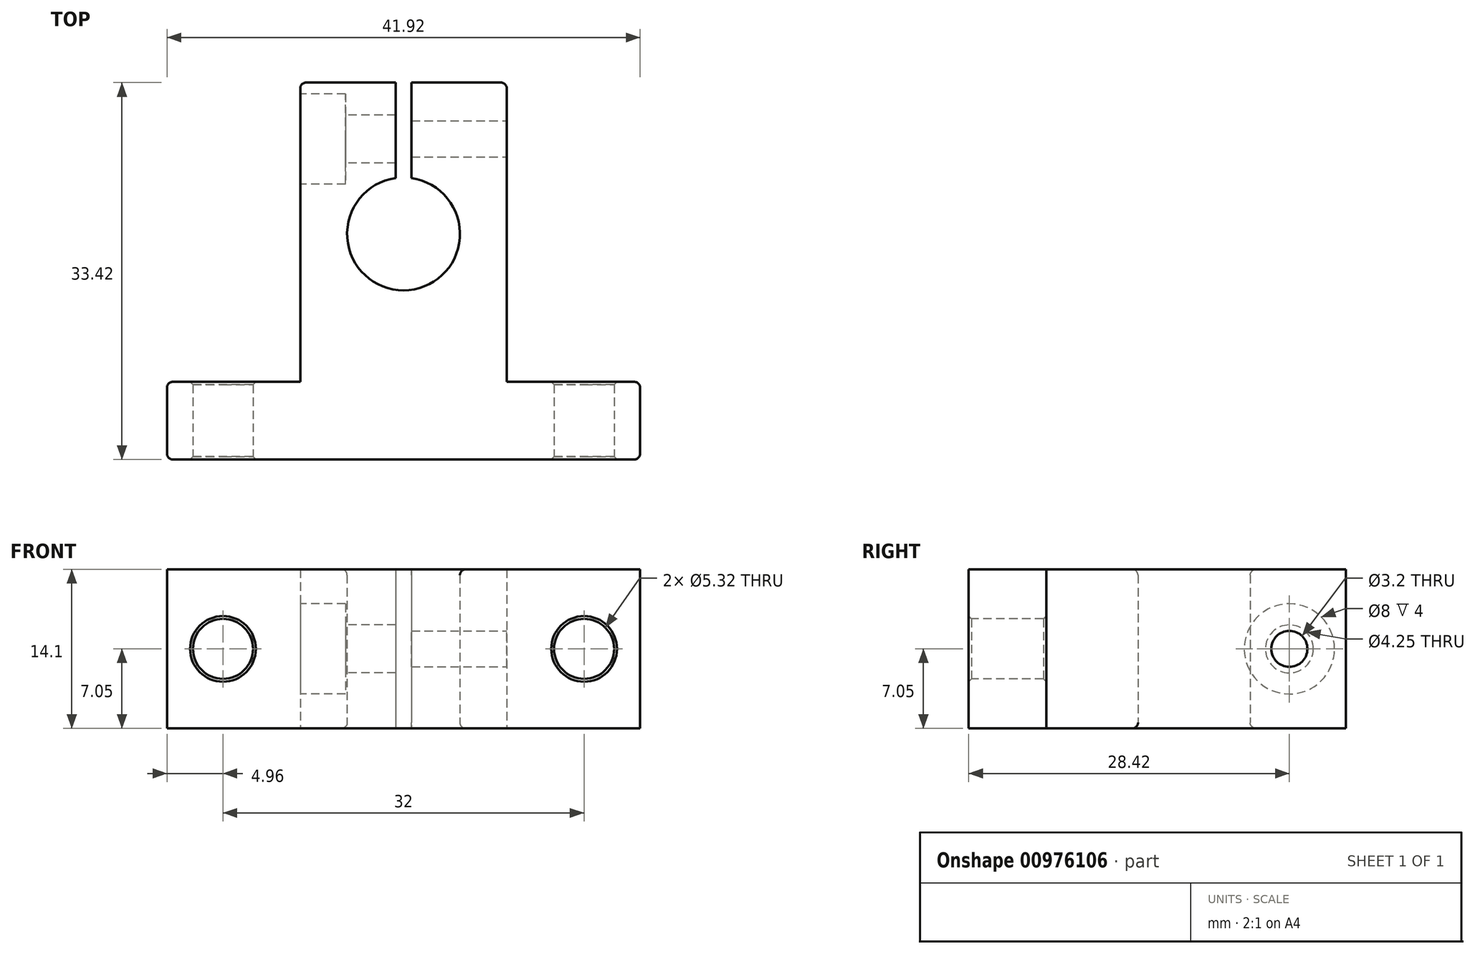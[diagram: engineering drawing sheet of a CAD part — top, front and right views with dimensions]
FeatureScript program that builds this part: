
annotation { "Feature Type Name" : "Feature", "Feature Type Description" : "" }
export const myFeature = defineFeature(function(context is Context, id is Id, definition is map)
    precondition{}
    {
        {
            var Q0;
            Q0=qCreatedBy(makeId("Top.planeOp"),FACE);
            var sketch = newSketch(context, id + "F0", { "sketchPlane" : qUnion([Q0])});
            skArc(sketch, "E0", {"start": v(-0.7, 4.95) * mm, "mid": v(0, -5) * mm, "end": v(0.7, 4.95) * mm});
            skLineSegment(sketch, "E1.bottom", {"start": v(-9.15, 13.42) * mm, "end": v(-0.7, 13.42) * mm});
            skLineSegment(sketch, "E1.left", {"start": v(-9.15, 13.42) * mm, "end": v(-9.15, -13.12) * mm});
            skLineSegment(sketch, "E1.right", {"start": v(9.15, 13.42) * mm, "end": v(9.15, -13.12) * mm});
            skLineSegment(sketch, "E2.bottom", {"start": v(-20.96, -13.12) * mm, "end": v(-9.15, -13.12) * mm});
            skLineSegment(sketch, "E2.top", {"start": v(-20.96, -20) * mm, "end": v(20.96, -20) * mm});
            skLineSegment(sketch, "E2.left", {"start": v(-20.96, -13.12) * mm, "end": v(-20.96, -20) * mm});
            skLineSegment(sketch, "E2.right", {"start": v(20.96, -13.12) * mm, "end": v(20.96, -20) * mm});
            skLineSegment(sketch, "E3.trimOffspring", {"start": v(9.15, -13.12) * mm, "end": v(20.96, -13.12) * mm});
            skLineSegment(sketch, "E4", {"start": v(0, 0) * mm, "end": v(0, 13.42) * mm, "construction": true});
            skLineSegment(sketch, "E5", {"start": v(0, 0) * mm, "end": v(0, -20) * mm, "construction": true});
            skLineSegment(sketch, "E6", {"start": v(-0.7, 4.95) * mm, "end": v(-0.7, 13.42) * mm});
            skLineSegment(sketch, "E7", {"start": v(0.7, 13.42) * mm, "end": v(0.7, 4.95) * mm});
            skLineSegment(sketch, "E8.trimOffspring", {"start": v(0.7, 13.42) * mm, "end": v(9.15, 13.42) * mm});
            skLineSegment(sketch, "E9", {"start": v(-0.7, 13.42) * mm, "end": v(0.7, 13.42) * mm, "construction": true});
            skSolve(sketch);
        }
        {
            var Q0;
            Q0 = qSketchRegion(id + "F0", true);
            extrude(context, id + "F1", {"entities" : qUnion([Q0]), "depth" : 14.1 * mm, "offsetDistance" : 25 * mm});
        }
        {
            var Q0;
            Q0=makeQuery(id+"F1.opExtrude","SWEPT_FACE",FACE,{"disambiguationData":[OSD([sQuery(id+"F0.wireOp",EDGE,"E1.right")])]});
            var sketch = newSketch(context, id + "F2", { "sketchPlane" : qUnion([Q0])});
            skLineSegment(sketch, "E10", {"start": v(8.42, 14.1) * mm, "end": v(8.42, 0) * mm, "construction": true});
            skCircle(sketch, "E11", {"center": v(8.42, 7.05) * mm, "radius": 1.6 * mm});
            skSolve(sketch);
        }
        {
            var Q0;
            Q0 = qSketchRegion(id + "F2", true);
            extrude(context, id + "F3", {"entities" : qUnion([Q0]), "operationType" : NewBodyOperationType.REMOVE, "endBound" : BoundingType.THROUGH_ALL, "oppositeDirection" : true, "depth" : 25 * mm, "offsetDistance" : 25 * mm});
        }
        {
            var Q0;
            Q0=makeQuery(id+"F1.opExtrude","SWEPT_FACE",FACE,{"disambiguationData":[OSD([sQuery(id+"F0.wireOp",EDGE,"E1.left")])]});
            var sketch = newSketch(context, id + "F4", { "sketchPlane" : qUnion([Q0])});
            skCircle(sketch, "E12", {"center": v(-8.42, 7.05) * mm, "radius": 4 * mm});
            skSolve(sketch);
        }
        {
            var Q0;
            Q0 = qSketchRegion(id + "F4", true);
            extrude(context, id + "F5", {"entities" : qUnion([Q0]), "operationType" : NewBodyOperationType.REMOVE, "oppositeDirection" : true, "depth" : 4 * mm, "offsetDistance" : 25 * mm});
        }
        {
            var Q0;
            Q0=makeQuery(id+"F1.opExtrude","SWEPT_FACE",FACE,{"disambiguationData":[OSD([sQuery(id+"F0.wireOp",EDGE,"E2.top")])]});
            var sketch = newSketch(context, id + "F6", { "sketchPlane" : qUnion([Q0])});
            skLineSegment(sketch, "E13", {"start": v(-20.96, 7.05) * mm, "end": v(-16, 7.05) * mm, "construction": true});
            skLineSegment(sketch, "E14", {"start": v(-16, 7.05) * mm, "end": v(16, 7.05) * mm, "construction": true});
            skLineSegment(sketch, "E15", {"start": v(16, 7.05) * mm, "end": v(20.96, 7.05) * mm, "construction": true});
            skCircle(sketch, "E16", {"center": v(-16, 7.05) * mm, "radius": 2.66 * mm});
            skCircle(sketch, "E17", {"center": v(16, 7.05) * mm, "radius": 2.66 * mm});
            skSolve(sketch);
        }
        {
            var Q0;
            Q0 = qSketchRegion(id + "F6", true);
            extrude(context, id + "F7", {"entities" : qUnion([Q0]), "operationType" : NewBodyOperationType.REMOVE, "oppositeDirection" : true, "depth" : 25 * mm, "offsetDistance" : 25 * mm});
        }
        {
            var Q0;
            Q0=makeQuery(id+"F5.boolean.opBoolean","COPY",FACE,{"derivedFrom":makeQuery(id+"F5.opExtrude","CAP_FACE",FACE,{"disambiguationData":[OSD([sQuery(id+"F4.wireOp",EDGE,"E12")])],"isStart":false})});
            var sketch = newSketch(context, id + "F8", { "sketchPlane" : qUnion([Q0])});
            skCircle(sketch, "E18", {"center": v(-8.42, 7.05) * mm, "radius": 2.12 * mm});
            skSolve(sketch);
        }
        {
            var Q0;
            Q0 = qSketchRegion(id + "F8", true);
            var Q1;
            Q1=makeQuery(id+"F1.opExtrude","SWEPT_FACE",FACE,{"disambiguationData":[OSD([sQuery(id+"F0.wireOp",EDGE,"E7")])]});
            extrude(context, id + "F9", {"entities" : qUnion([Q0]), "operationType" : NewBodyOperationType.REMOVE, "endBound" : BoundingType.UP_TO_SURFACE, "oppositeDirection" : true, "depth" : 25 * mm, "endBoundEntityFace" : qUnion([Q1]), "offsetDistance" : 25 * mm});
        }
        {
            var Q0;
            Q0=makeQuery(id+"F1.opExtrude","SWEPT_EDGE",EDGE,{"disambiguationData":[OSD([sQuery(id+"F0.wireOp",EDGE,"E2.bottom"),sQuery(id+"F0.wireOp",EDGE,"E2.left")])]});
            var Q1;
            Q1=makeQuery(id+"F1.opExtrude","SWEPT_EDGE",EDGE,{"disambiguationData":[OSD([sQuery(id+"F0.wireOp",EDGE,"E2.top"),sQuery(id+"F0.wireOp",EDGE,"E2.left")])]});
            var Q2;
            Q2=makeQuery(id+"F1.opExtrude","SWEPT_EDGE",EDGE,{"disambiguationData":[OSD([sQuery(id+"F0.wireOp",EDGE,"E2.right"),sQuery(id+"F0.wireOp",EDGE,"E3.trimOffspring")])]});
            var Q3;
            Q3=makeQuery(id+"F1.opExtrude","SWEPT_EDGE",EDGE,{"disambiguationData":[OSD([sQuery(id+"F0.wireOp",EDGE,"E2.top"),sQuery(id+"F0.wireOp",EDGE,"E2.right")])]});
            var Q4;
            Q4=makeQuery(id+"F1.opExtrude","SWEPT_EDGE",EDGE,{"disambiguationData":[OSD([sQuery(id+"F0.wireOp",EDGE,"E1.right"),sQuery(id+"F0.wireOp",EDGE,"E8.trimOffspring")])]});
            var Q5;
            Q5=makeQuery(id+"F1.opExtrude","SWEPT_EDGE",EDGE,{"disambiguationData":[OSD([sQuery(id+"F0.wireOp",EDGE,"E1.bottom"),sQuery(id+"F0.wireOp",EDGE,"E1.left")])]});
            var Q6;
            Q6=makeQuery(id+"F1.opExtrude","CAP_EDGE",EDGE,{"disambiguationData":[OSD([sQuery(id+"F0.wireOp",EDGE,"E0")])],"isStart":false});
            var Q7;
            Q7=makeQuery(id+"F1.opExtrude","CAP_EDGE",EDGE,{"disambiguationData":[OSD([sQuery(id+"F0.wireOp",EDGE,"E0")])],"isStart":true});
            fillet(context, id + "F10", {"entities" : qUnion([Q0, Q1, Q2, Q3, Q4, Q5, Q6, Q7]), "radius" : .5 * mm, "tangentPropagation" : true, "allowEdgeOverflow" : false});
        }
        {
            var Q0;
            Q0=makeQuery(id+"F7.boolean.opBoolean","COPY",FACE,{"derivedFrom":makeQuery(id+"F7.opExtrude","SWEPT_FACE",FACE,{"disambiguationData":[OSD([sQuery(id+"F6.wireOp",EDGE,"E17")])]})});
            var Q1;
            Q1=makeQuery(id+"F7.boolean.opBoolean","COPY",FACE,{"derivedFrom":makeQuery(id+"F7.opExtrude","SWEPT_FACE",FACE,{"disambiguationData":[OSD([sQuery(id+"F6.wireOp",EDGE,"E16")])]})});
            chamfer(context, id + "F11", {"entities" : qUnion([Q0, Q1]), "width" : .25 * mm, "tangentPropagation" : true});
        }
    });
